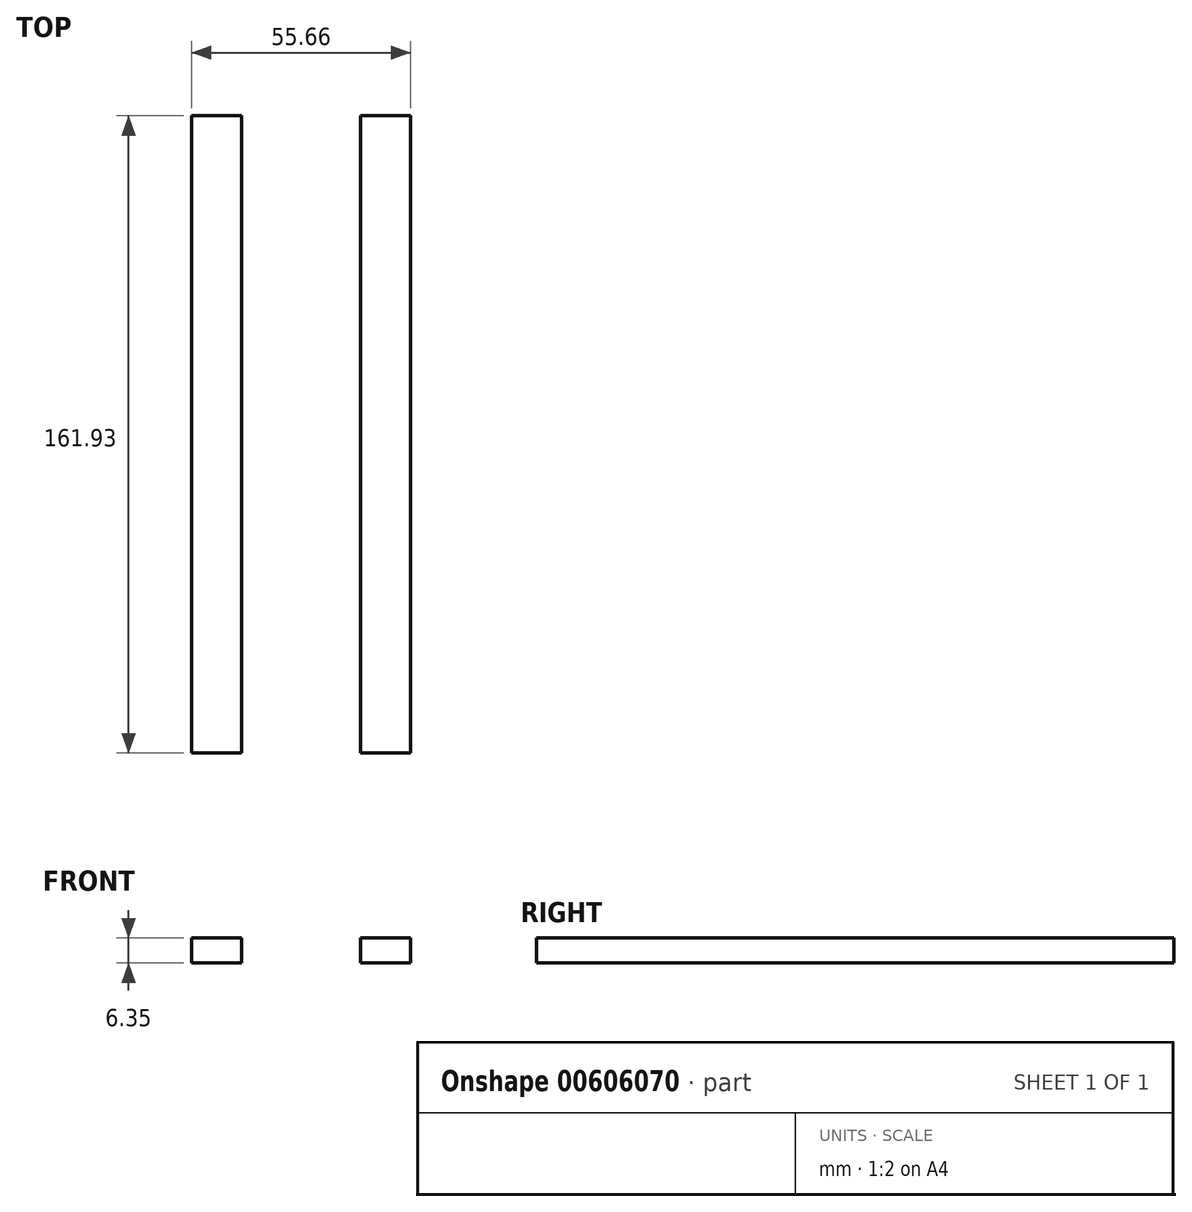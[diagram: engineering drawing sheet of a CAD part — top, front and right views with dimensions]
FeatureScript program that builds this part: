
annotation { "Feature Type Name" : "Feature", "Feature Type Description" : "" }
export const myFeature = defineFeature(function(context is Context, id is Id, definition is map)
    precondition{}
    {
        {
            var Q0;
            Q0=qCreatedBy(makeId("Top.planeOp"),FACE);
            var sketch = newSketch(context, id + "F0", { "sketchPlane" : qUnion([Q0])});
            skLineSegment(sketch, "E0.bottom", {"start": v(0, 0) * mm, "end": v(12.7, 0) * mm});
            skLineSegment(sketch, "E0.top", {"start": v(0, 161.93) * mm, "end": v(12.7, 161.93) * mm});
            skLineSegment(sketch, "E0.left", {"start": v(0, 0) * mm, "end": v(0, 161.93) * mm});
            skLineSegment(sketch, "E0.right", {"start": v(12.7, 0) * mm, "end": v(12.7, 161.93) * mm});
            skLineSegment(sketch, "E1.bottom", {"start": v(42.96, 0) * mm, "end": v(55.66, 0) * mm});
            skLineSegment(sketch, "E1.top", {"start": v(42.96, 161.93) * mm, "end": v(55.66, 161.93) * mm});
            skLineSegment(sketch, "E1.left", {"start": v(42.96, 0) * mm, "end": v(42.96, 161.93) * mm});
            skLineSegment(sketch, "E1.right", {"start": v(55.66, 0) * mm, "end": v(55.66, 161.93) * mm});
            skSolve(sketch);
        }
        {
            var Q0;
            Q0=makeQuery(id+"F0.imprint","IMPRINT",FACE,{"disambiguationData":[TD([[makeQuery(id+"F0.imprint","IMPRINT",EDGE,{"derivedFrom":sQuery(id+"F0.wireOp",EDGE,"E0.bottom")}),1.0]])]});
            var Q1;
            Q1=makeQuery(id+"F0.imprint","IMPRINT",FACE,{"disambiguationData":[TD([[makeQuery(id+"F0.imprint","IMPRINT",EDGE,{"derivedFrom":sQuery(id+"F0.wireOp",EDGE,"E1.bottom")}),1.0]])]});
            extrude(context, id + "F1", {"entities" : qUnion([Q0, Q1]), "depth" : 6.35 * mm, "offsetDistance" : 25.4 * mm});
        }
    });
